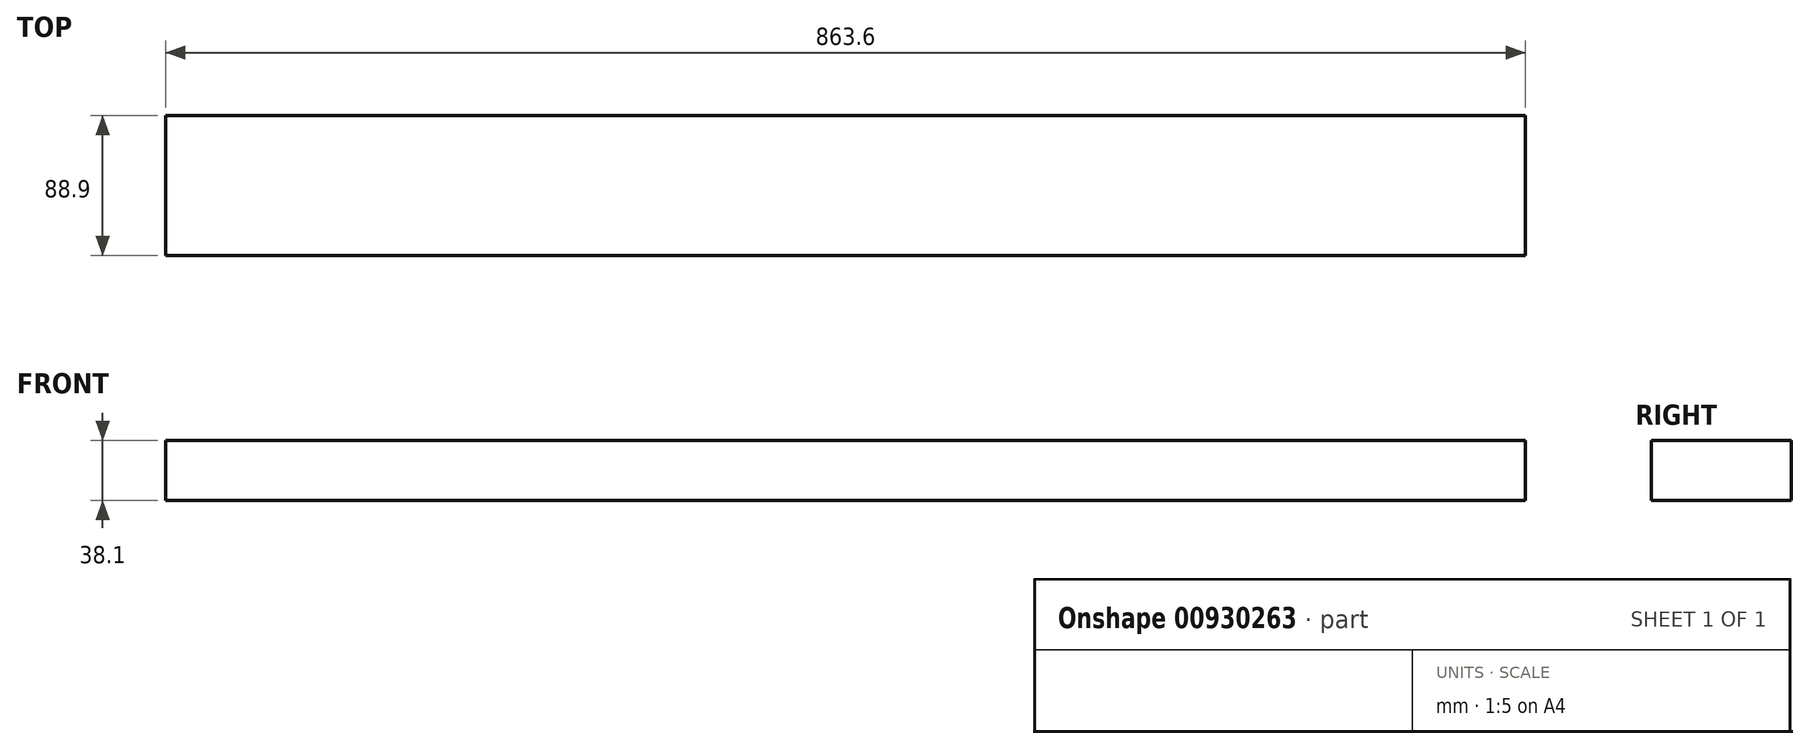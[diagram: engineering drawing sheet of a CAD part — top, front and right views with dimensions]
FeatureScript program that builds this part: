
annotation { "Feature Type Name" : "Feature", "Feature Type Description" : "" }
export const myFeature = defineFeature(function(context is Context, id is Id, definition is map)
    precondition{}
    {
        {
            var Q0;
            Q0=qCreatedBy(makeId("Right.planeOp"),FACE);
            var sketch = newSketch(context, id + "F0", { "sketchPlane" : qUnion([Q0])});
            skLineSegment(sketch, "E0.bottom", {"start": v(44.45, -19.05) * mm, "end": v(-44.45, -19.05) * mm});
            skLineSegment(sketch, "E0.top", {"start": v(44.45, 19.05) * mm, "end": v(-44.45, 19.05) * mm});
            skLineSegment(sketch, "E0.left", {"start": v(44.45, -19.05) * mm, "end": v(44.45, 19.05) * mm});
            skLineSegment(sketch, "E0.right", {"start": v(-44.45, -19.05) * mm, "end": v(-44.45, 19.05) * mm});
            skPoint(sketch, "E0.middle", {"position": v(0, 0) * mm});
            skSolve(sketch);
        }
        {
            var Q0;
            Q0=qSketchRegion(id+"F0",true);
            extrude(context, id + "F1", {"entities" : qUnion([Q0]), "endBound" : BoundingType.SYMMETRIC, "depth" : 863.6 * mm});
        }
    });
